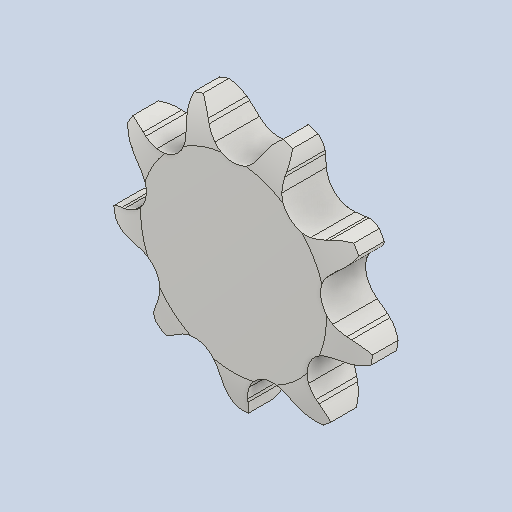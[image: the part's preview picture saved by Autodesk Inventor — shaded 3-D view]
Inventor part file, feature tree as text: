
AUTODESK INVENTOR PART (.ipt)
format: ipt  version: 2022.1 (Build 261234000, 234)  size: 371,712 bytes
history: native  units: mm
features: other x6, extrude x2, pattern_linear x1, pattern_circular x1
ambient origin geometry x8: Origin, YZ Plane, XZ Plane, XY Plane, X Axis, Y Axis, Z Axis, Center Point
bodies: Solid1 (feature_tree)
feature tree (10):
  other  "Perfil de diente teórico"
  other  "Perfil de diente"
  other  "Perfil de sección"
  other  "Cubierta"
  other  "Ramal"
  pattern_linear  "Patrón de ramal"  Spacing1=46.415395mm  [1 undecoded]
  extrude  "Diente teórico"  Depth=6.981317mm
  extrude  "Diente"  Depth=5.1308mm
  pattern_circular  "Patrón de diente"  [2 undecoded]
  other  "Plano síncrono"
note: 3 required parameter values undecoded (feature->parameter linkage not recoverable at this tier; creation-order binding heuristic only, values carry confidence <= 0.55)
